# Revit family: Plumbing-Fix_Faucet-Touchless_Stern_Malmo
name_source: partatom
category: Plumbing Fixtures
revit_build: Autodesk Revit 2015 (Build: 20140606_1530(x64)
units: mm (PartAtom-declared; Revit-internal decimal feet)

## types (5) — shared parameters
Assembly Code = D2010300
Available Options = as Specified
Body Construction = Brass
CW Connection = Yes
CWFU = 1
Default Elevation = 0' - 0"
Description = Stern Touchless Wall Mounted Faucet - Malmo B as Specified
HW Connection = Yes
HWFU = 1
Keynote = 22 40 00
Manufacturer = Stern Engineering
Manufacturer Website = http://www.sternfaucets.com
Model = Malmo B
Operating Pressure Range = 7.26 - 116 PSI  ;  0.5 - 8 bar
Operating Temperature Range = Up to 149 F / 65 C
Piping_Inlet Diameter = 1"
Power Supply = 9V Battery
Product Data = http://www.arcat.com
Product Features = as Specified
Revision = R1_2018-04
Sales Information = http://www.sternfaucets.com
Spout Height = 0' - 2 1/4"
Spout Reach = 0' - 8"
Standards Conformance = as Specified
Type Comments = as Specified
URL = http://www.sternfaucets.com
Unit Height = 0' - 8 5/8"
Unit Width = 0' - 2"
Vent Connection = No
Warranty Duration (Years) = 2
Waste Connection = No
zero-valued in all types: Cost, Expected Lifespan (Years), Maintenance Schedule (Months), WFU

## per-type parameters (varying)
| type | Piping_Flow |
| 1.58 GPM | 2 GPM |
| 1 GPM | 1 GPM |
| 0.8 GPM | 1 GPM |
| 0.5 GPM | 1 GPM |
| 0.35 GPM | 0 GPM |

## geometry (parser evidence)
native form markers: Sweep x3
no freeform markers — native parametric forms only
